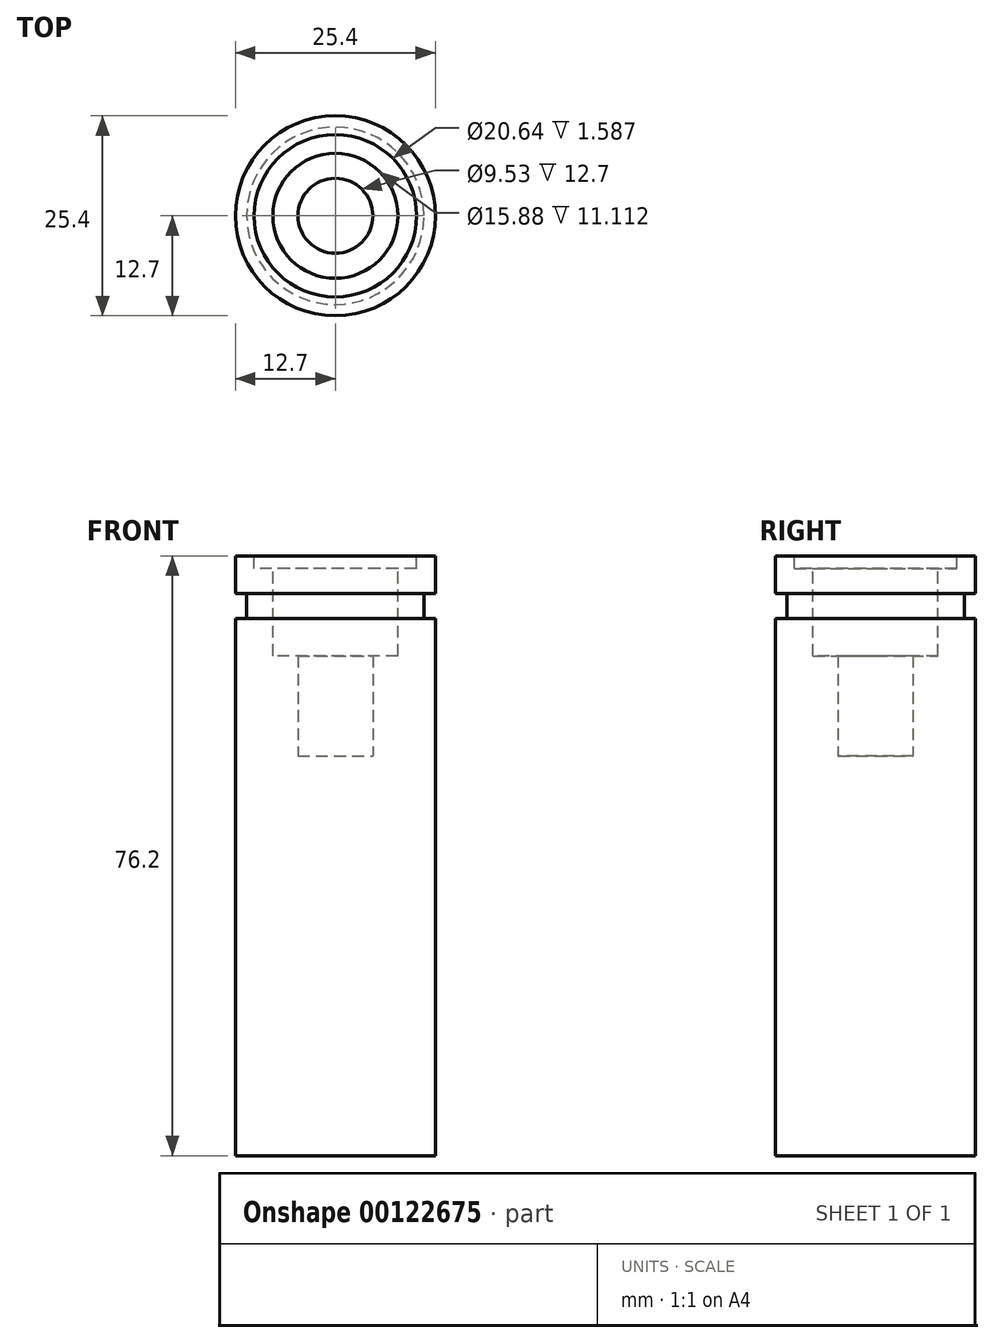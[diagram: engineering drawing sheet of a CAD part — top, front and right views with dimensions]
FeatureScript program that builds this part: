
annotation { "Feature Type Name" : "Feature", "Feature Type Description" : "" }
export const myFeature = defineFeature(function(context is Context, id is Id, definition is map)
    precondition{}
    {
        {
            var Q0;
            Q0=qCreatedBy(makeId("Right.planeOp"),FACE);
            var sketch = newSketch(context, id + "F0", { "sketchPlane" : qUnion([Q0])});
            skLineSegment(sketch, "E0", {"start": v(12.7, 0) * mm, "end": v(12.7, -4.76) * mm});
            skLineSegment(sketch, "E1", {"start": v(12.7, -4.76) * mm, "end": v(11.27, -4.76) * mm});
            skLineSegment(sketch, "E2", {"start": v(11.27, -4.76) * mm, "end": v(11.27, -7.94) * mm});
            skLineSegment(sketch, "E3", {"start": v(11.27, -7.94) * mm, "end": v(12.7, -7.94) * mm});
            skLineSegment(sketch, "E4", {"start": v(12.7, -7.94) * mm, "end": v(12.7, -76.2) * mm});
            skLineSegment(sketch, "E5", {"start": v(12.7, -76.2) * mm, "end": v(0, -76.2) * mm});
            skLineSegment(sketch, "E6", {"start": v(0, -83.03) * mm, "end": v(0, 15.65) * mm});
            skLineSegment(sketch, "E7", {"start": v(12.7, 0) * mm, "end": v(4.76, 0) * mm});
            skLineSegment(sketch, "E8", {"start": v(4.76, 0) * mm, "end": v(4.76, -25.4) * mm});
            skLineSegment(sketch, "E9", {"start": v(4.76, -25.4) * mm, "end": v(0, -25.4) * mm});
            skSolve(sketch);
        }
        {
            var Q0;
            Q0=makeQuery(id+"F0.imprint","IMPRINT",FACE,{"disambiguationData":[TD([[makeQuery(id+"F0.imprint","IMPRINT",EDGE,{"derivedFrom":sQuery(id+"F0.wireOp",EDGE,"E0")}),-1.0]])]});
            var Q1;
            Q1=sQuery(id+"F0.wireOp",EDGE,"E6");
            revolve(context, id + "F1", {"entities" : qUnion([Q0]), "axis" : qUnion([Q1]), "revolveType" : RevolveType.FULL});
        }
        {
            var Q0;
            Q0=makeQuery(id+"F1.opRevolve","SWEPT_FACE",FACE,{"disambiguationData":[OSD([sQuery(id+"F0.wireOp",EDGE,"E7")])]});
            var sketch = newSketch(context, id + "F2", { "sketchPlane" : qUnion([Q0])});
            skCircle(sketch, "E10", {"center": v(0, 0) * mm, "radius": 7.94 * mm});
            skSolve(sketch);
        }
        {
            var Q0;
            Q0=makeQuery(id+"F2.imprint","IMPRINT",FACE,{"disambiguationData":[TD([[makeQuery(id+"F2.imprint","IMPRINT",EDGE,{"derivedFrom":sQuery(id+"F2.wireOp",EDGE,"E10")}),1.0]])]});
            extrude(context, id + "F3", {"entities" : qUnion([Q0]), "operationType" : NewBodyOperationType.REMOVE, "oppositeDirection" : true, "depth" : 12.7 * mm});
        }
        {
            var Q0;
            Q0=makeQuery(id+"F1.opRevolve","SWEPT_FACE",FACE,{"disambiguationData":[OSD([sQuery(id+"F0.wireOp",EDGE,"E7")])]});
            var sketch = newSketch(context, id + "F4", { "sketchPlane" : qUnion([Q0])});
            skCircle(sketch, "E11", {"center": v(0, 0) * mm, "radius": 10.32 * mm});
            skSolve(sketch);
        }
        {
            var Q0;
            Q0=makeQuery(id+"F4.imprint","IMPRINT",FACE,{"disambiguationData":[TD([[makeQuery(id+"F4.imprint","IMPRINT",EDGE,{"derivedFrom":sQuery(id+"F4.wireOp",EDGE,"E11")}),1.0]])]});
            extrude(context, id + "F5", {"entities" : qUnion([Q0]), "operationType" : NewBodyOperationType.REMOVE, "oppositeDirection" : true, "depth" : 1.59 * mm});
        }
    });
